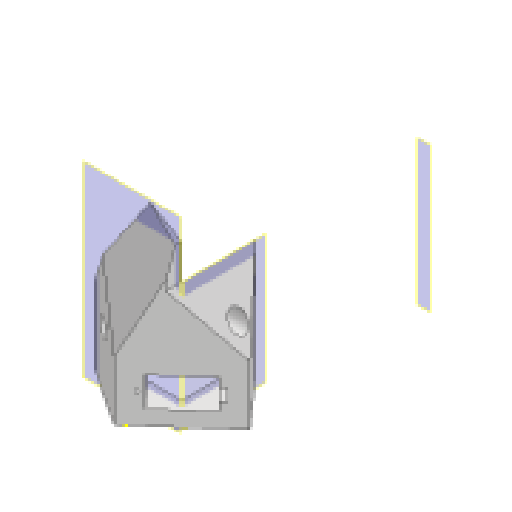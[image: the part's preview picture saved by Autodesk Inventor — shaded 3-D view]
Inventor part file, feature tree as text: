
AUTODESK INVENTOR PART (.ipt)
format: ipt  version: 2025 (Build 290162010, 162A)  size: 235,008 bytes
history: native  units: in
note: dims shown in document units (in); Inventor stores cm internally (conversion verified against a paired STEP export)
features: sketch x17, extrude x16, reference x10, other x5, plane x3, projected_geometry x2, chamfer x1
ambient origin geometry x8: Origin, YZ Plane, XZ Plane, XY Plane, X Axis, Y Axis, Z Axis, Center Point
bodies: Solid1 (feature_tree)
feature tree (54):
  extrude  "Extrusion1"  Depth=1.0in
  extrude  "Extrusion2"  Depth=1.0in TaperAngle=0.0deg
  extrude  "Extrusion3"  Depth=0.2in TaperAngle=0.0deg
  sketch  "Sketch4"  dims[d9=0.5in d10=0.9in]
  extrude  "Extrusion4"  Depth=0.9in
  extrude  "Extrusion6"  Depth=0.1in
  extrude  "Extrusion7"  Depth=0.2in TaperAngle=0.0deg
  extrude  "Extrusion8"  Depth=2.9375in TaperAngle=0.0deg
  extrude  "Extrusion9"  Depth=1.0in TaperAngle=0.0deg
  plane  "Work Plane1"
  extrude  "Extrusion10"  Depth=1.0in TaperAngle=0.0deg
  extrude  "Extrusion11"  Depth=0.505in
  plane  "Work Plane2"
  extrude  "Extrusion12"  Depth=0.6in TaperAngle=0.0deg
  extrude  "Extrusion13"  Depth=0.3in
  plane  "Work Plane3"
  extrude  "Extrusion14"  Depth=0.14in
  extrude  "Extrusion15"  Depth=1.0in
  extrude  "Extrusion16"  [1 undecoded]
  extrude  "Extrusion18"  Depth=0.6in TaperAngle=0.0deg
  chamfer  "Chamfer1"  Distance=0.6in
  sketch  "Sketch1"  dims[d0=1.5in d2=1.0in]
  sketch  "Sketch2"  dims[d3=1.125in d4=1.0in d5=0.0in]
  sketch  "Sketch3"  dims[d6=0.2in d7=1.9375in d8=0.0in]
  sketch  "Sketch5"  dims[d11=3.25in d12=0.0in d13=0.1in]
  sketch  "Sketch7"  dims[d14=0.2in d15=1.4375in d16=0.0in]
  reference  "Reference1"
  reference  "Reference2"
  reference  "Reference3"
  reference  "Reference4"
  sketch  "Sketch8"  dims[d19=0.8125in d20=0.0in d21=2.9375in d22=0.0in]
  projected_geometry  "Projected Loop1"
  sketch  "Sketch9"  dims[d23=3.625in d24=0.0in d25=1.0in d26=0.0in]
  sketch  "Sketch10"  dims[d27=1.0in d28=8.25in d29=0.0in]
  projected_geometry  "Projected Loop2"
  reference  "Reference5"
  reference  "Reference6"
  reference  "Reference7"
  sketch  "Sketch11"  dims[d30=0.14in d31=0.505in]
  sketch  "Sketch12"  dims[d32=0.6in d33=8.25in d34=0.0in]
  reference  "Reference8"
  sketch  "Sketch13"  dims[d35=-0.1in d36=0.3in]
  sketch  "Sketch14"  dims[d37=8.25in d38=0.0in d39=0.14in]
  sketch  "Sketch15"  dims[d40=0.5in d41=1.0in]
  sketch  "Sketch16"  dims[d42=4.5625in d43=0.0in d44=-0.1in]
  reference  "Reference9"
  sketch  "Sketch17"  dims[d45=0.3in d46=4.5625in d47=0.0in d48=0.6in d49=0.0in]
  sketch  "Sketch19"  dims[d50=1.1in d51=0.07in d52=0.07in d53=0.55in d54=0.15in d55=0.0in d58=0.3in d59=0.0in d60=0.0625in d61=0.125in d62=45.0deg]
  reference  "Reference13"
  parser-record x1  (decoder bookkeeping rows leaked as tree rows — omitted from the tree; the rows remain in map.json)
  other  "Hand Assem.iam"
  other  "PALM 4:1"
  other  "Palm:1"
  other  "Wrist Base:1"
note: 1 required parameter value undecoded (feature->parameter linkage not recoverable at this tier; creation-order binding heuristic only, values carry confidence <= 0.55)
note: 1 file-system path scrubbed to <path> (originals preserved in map.json)
